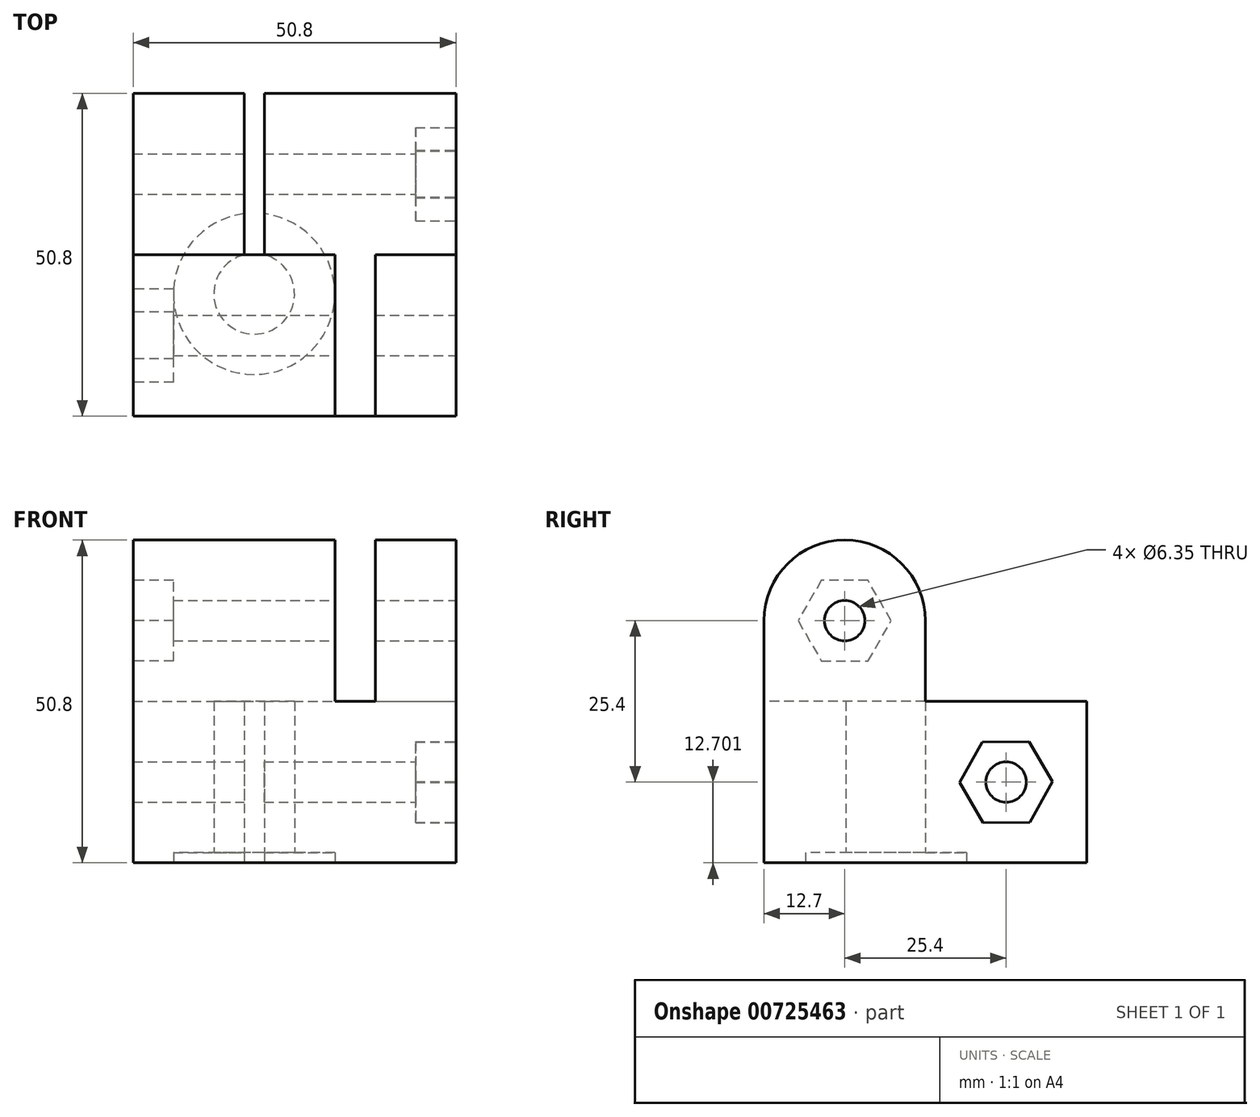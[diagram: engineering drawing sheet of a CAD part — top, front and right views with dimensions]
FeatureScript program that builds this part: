
annotation { "Feature Type Name" : "Feature", "Feature Type Description" : "" }
export const myFeature = defineFeature(function(context is Context, id is Id, definition is map)
    precondition{}
    {
        {
            var Q0;
            Q0=qCreatedBy(makeId("Front.planeOp"),FACE);
            var sketch = newSketch(context, id + "F0", { "sketchPlane" : qUnion([Q0])});
            skLineSegment(sketch, "E0.bottom", {"start": v(-27.31, 27.37) * mm, "end": v(23.49, 27.37) * mm});
            skLineSegment(sketch, "E0.top", {"start": v(-27.31, -23.43) * mm, "end": v(23.49, -23.43) * mm});
            skLineSegment(sketch, "E0.left", {"start": v(-27.31, 27.37) * mm, "end": v(-27.31, -23.43) * mm});
            skLineSegment(sketch, "E0.right", {"start": v(23.49, 27.37) * mm, "end": v(23.49, -23.43) * mm});
            skSolve(sketch);
        }
        {
            var Q0;
            Q0=makeQuery(id+"F0.imprint","IMPRINT",FACE,{"disambiguationData":[TD([[makeQuery(id+"F0.imprint","IMPRINT",EDGE,{"derivedFrom":sQuery(id+"F0.wireOp",EDGE,"E0.bottom")}),-1.0]])]});
            extrude(context, id + "F1", {"entities" : qUnion([Q0]), "endBound" : BoundingType.SYMMETRIC, "depth" : 50.8 * mm, "offsetDistance" : 25.4 * mm});
        }
        {
            var Q0;
            Q0=makeQuery(id+"F1.opExtrude","SWEPT_FACE",FACE,{"disambiguationData":[OSD([sQuery(id+"F0.wireOp",EDGE,"E0.top")])]});
            var sketch = newSketch(context, id + "F2", { "sketchPlane" : qUnion([Q0])});
            skArc(sketch, "E1", {"start": v(-6.67, 0) * mm, "mid": v(-8.26, 12.5) * mm, "end": v(-9.85, 0) * mm});
            skLineSegment(sketch, "E2.top", {"start": v(-9.85, -25.4) * mm, "end": v(-6.67, -25.4) * mm});
            skLineSegment(sketch, "E2.left", {"start": v(-9.85, 0) * mm, "end": v(-9.85, -25.4) * mm});
            skLineSegment(sketch, "E2.right", {"start": v(-6.67, 0) * mm, "end": v(-6.67, -25.4) * mm});
            skCircle(sketch, "E3", {"center": v(-8.26, 6.15) * mm, "radius": 12.7 * mm});
            skSolve(sketch);
        }
        {
            var Q0;
            Q0=makeQuery(id+"F2.imprint","IMPRINT",FACE,{"disambiguationData":[TD([[makeQuery(id+"F2.imprint","IMPRINT",EDGE,{"derivedFrom":sQuery(id+"F2.wireOp",EDGE,"E1")}),1.0]])]});
            var Q1;
            {var subQ0=sQuery(id+"F2.wireOp",EDGE,"E2.top");Q1=makeQuery(id+"F2.imprint","IMPRINT",FACE,{"disambiguationData":[TD([[makeQuery(id+"F2.imprint","IMPRINT",EDGE,{"derivedFrom":subQ0}),1.0]])]});}
            extrude(context, id + "F3", {"entities" : qUnion([Q0, Q1]), "operationType" : NewBodyOperationType.REMOVE, "oppositeDirection" : true, "depth" : 25.4 * mm, "offsetDistance" : 25.4 * mm});
        }
        {
            var Q0;
            Q0=makeQuery(id+"F1.opExtrude","SWEPT_FACE",FACE,{"disambiguationData":[OSD([sQuery(id+"F0.wireOp",EDGE,"E0.right")])]});
            var sketch = newSketch(context, id + "F4", { "sketchPlane" : qUnion([Q0])});
            skLineSegment(sketch, "E4", {"start": v(-36.89, 1.97) * mm, "end": v(-36.89, 33.76) * mm});
            skLineSegment(sketch, "E5", {"start": v(-36.89, 33.76) * mm, "end": v(34.59, 33.76) * mm});
            skLineSegment(sketch, "E6", {"start": v(34.59, 33.76) * mm, "end": v(34.59, 1.97) * mm});
            skArc(sketch, "E7", {"start": v(0, 14.67) * mm, "mid": v(-12.7, 27.37) * mm, "end": v(-25.4, 14.67) * mm});
            skLineSegment(sketch, "E8", {"start": v(-25.4, 1.97) * mm, "end": v(-25.4, 14.67) * mm});
            skLineSegment(sketch, "E9", {"start": v(0, 1.97) * mm, "end": v(0, 14.67) * mm});
            skLineSegment(sketch, "E10", {"start": v(-36.89, 1.97) * mm, "end": v(34.59, 1.97) * mm});
            skPoint(sketch, "E11.orphan", {"position": v(-25.4, 0) * mm});
            skPoint(sketch, "E12.orphan", {"position": v(34.59, 0) * mm});
            skCircle(sketch, "E13", {"center": v(-12.7, 14.67) * mm, "radius": 3.18 * mm});
            skCircle(sketch, "E14", {"center": v(12.7, -10.73) * mm, "radius": 3.18 * mm});
            skCircle(sketch, "E15.cCircle", {"center": v(12.7, -10.73) * mm, "radius": 6.35 * mm, "construction": true});
            skLineSegment(sketch, "E15.0", {"start": v(20.03, -10.66) * mm, "end": v(16.43, -17.04) * mm});
            skLineSegment(sketch, "E15.1", {"start": v(16.43, -17.04) * mm, "end": v(9.1, -17.11) * mm});
            skLineSegment(sketch, "E15.2", {"start": v(9.1, -17.11) * mm, "end": v(5.37, -10.8) * mm});
            skLineSegment(sketch, "E15.3", {"start": v(5.37, -10.8) * mm, "end": v(8.97, -4.41) * mm});
            skLineSegment(sketch, "E15.4", {"start": v(8.97, -4.41) * mm, "end": v(16.3, -4.34) * mm});
            skLineSegment(sketch, "E15.5", {"start": v(16.3, -4.34) * mm, "end": v(20.03, -10.66) * mm});
            skPoint(sketch, "E15.0.midPoint", {"position": v(18.23, -13.85) * mm});
            skSolve(sketch);
        }
        {
            var Q0;
            Q0=makeQuery(id+"F4.imprint","IMPRINT",FACE,{"disambiguationData":[TD([[makeQuery(id+"F4.imprint","IMPRINT",EDGE,{"derivedFrom":sQuery(id+"F4.wireOp",EDGE,"nHS85Hnr-vWbH-LP3G-OHDl-IovvBqo1vg3n")}),-1.0]])]});
            var Q1;
            {var subQ0=sQuery(id+"F4.wireOp",EDGE,"E7");var subQ1=sQuery(id+"F0.wireOp",EDGE,"E0.right");var subQ2=makeQuery(id+"F1.opExtrude","CAP_EDGE",EDGE,{"disambiguationData":[OSD([subQ1])],"isStart":false});var subQ3=makeQuery(id+"F4.imprint","INTERSECT",VERTEX,{"derivedFrom":[subQ2,subQ0,sQuery(id+"F4.wireOp",EDGE,"E8")]});Q1=makeQuery(id+"F4.imprint","IMPRINT",FACE,{"disambiguationData":[TD([[makeQuery(id+"F4.imprint","IMPRINT",EDGE,{"disambiguationData":[TD([[subQ3,1.0]])],"derivedFrom":subQ0}),-1.0]])]});}
            var Q2;
            {var subQ0=sQuery(id+"F4.wireOp",EDGE,"E9");Q2=makeQuery(id+"F4.imprint","IMPRINT",FACE,{"disambiguationData":[TD([[makeQuery(id+"F4.imprint","IMPRINT",EDGE,{"derivedFrom":subQ0}),-1.0]])]});}
            var Q3;
            Q3=makeQuery(id+"F4.imprint","IMPRINT",FACE,{"disambiguationData":[TD([[makeQuery(id+"F4.imprint","IMPRINT",EDGE,{"derivedFrom":sQuery(id+"F4.wireOp",EDGE,"E13")}),1.0]])]});
            var Q4;
            Q4=makeQuery(id+"F4.imprint","IMPRINT",FACE,{"disambiguationData":[TD([[makeQuery(id+"F4.imprint","IMPRINT",EDGE,{"derivedFrom":sQuery(id+"F4.wireOp",EDGE,"E14")}),1.0]])]});
            extrude(context, id + "F5", {"entities" : qUnion([Q0, Q1, Q2, Q3, Q4]), "operationType" : NewBodyOperationType.REMOVE, "endBound" : BoundingType.THROUGH_ALL, "oppositeDirection" : true, "depth" : 50.8 * mm, "offsetDistance" : 25.4 * mm});
        }
        {
            var Q0;
            Q0=makeQuery(id+"F1.opExtrude","CAP_FACE",FACE,{"disambiguationData":[OSD([sQuery(id+"F0.wireOp",EDGE,"E0.bottom"),sQuery(id+"F0.wireOp",EDGE,"E0.top"),sQuery(id+"F0.wireOp",EDGE,"E0.left"),sQuery(id+"F0.wireOp",EDGE,"E0.right")])],"isStart":false});
            var sketch = newSketch(context, id + "F6", { "sketchPlane" : qUnion([Q0])});
            skLineSegment(sketch, "E16.bottom", {"start": v(4.44, 1.97) * mm, "end": v(10.79, 1.97) * mm});
            skLineSegment(sketch, "E16.top", {"start": v(4.44, 44.67) * mm, "end": v(10.79, 44.67) * mm});
            skLineSegment(sketch, "E16.left", {"start": v(4.44, 1.97) * mm, "end": v(4.44, 44.67) * mm});
            skLineSegment(sketch, "E16.right", {"start": v(10.79, 1.97) * mm, "end": v(10.79, 44.67) * mm});
            skSolve(sketch);
        }
        {
            var Q0;
            {var subQ0=sQuery(id+"F6.wireOp",EDGE,"E16.top");Q0=makeQuery(id+"F6.imprint","IMPRINT",FACE,{"disambiguationData":[TD([[makeQuery(id+"F6.imprint","IMPRINT",EDGE,{"derivedFrom":subQ0}),-1.0]])]});}
            var Q1;
            {var subQ0=sQuery(id+"F6.wireOp",EDGE,"E16.bottom");Q1=makeQuery(id+"F6.imprint","IMPRINT",FACE,{"disambiguationData":[TD([[makeQuery(id+"F6.imprint","IMPRINT",EDGE,{"derivedFrom":subQ0}),1.0]])]});}
            extrude(context, id + "F7", {"entities" : qUnion([Q0, Q1]), "operationType" : NewBodyOperationType.REMOVE, "endBound" : BoundingType.THROUGH_ALL, "oppositeDirection" : true, "depth" : 25.4 * mm, "offsetDistance" : 25.4 * mm});
        }
        {
            var Q0;
            Q0=makeQuery(id+"F1.opExtrude","SWEPT_FACE",FACE,{"disambiguationData":[OSD([sQuery(id+"F0.wireOp",EDGE,"E0.left")])]});
            var sketch = newSketch(context, id + "F8", { "sketchPlane" : qUnion([Q0])});
            skCircle(sketch, "E17.cCircle", {"center": v(12.7, 14.67) * mm, "radius": 6.35 * mm, "construction": true});
            skLineSegment(sketch, "E17.0", {"start": v(5.37, 14.67) * mm, "end": v(9.03, 21.02) * mm});
            skLineSegment(sketch, "E17.1", {"start": v(9.03, 21.02) * mm, "end": v(16.37, 21.02) * mm});
            skLineSegment(sketch, "E17.2", {"start": v(16.37, 21.02) * mm, "end": v(20.03, 14.67) * mm});
            skLineSegment(sketch, "E17.3", {"start": v(20.03, 14.67) * mm, "end": v(16.37, 8.32) * mm});
            skLineSegment(sketch, "E17.4", {"start": v(16.37, 8.32) * mm, "end": v(9.03, 8.32) * mm});
            skLineSegment(sketch, "E17.5", {"start": v(9.03, 8.32) * mm, "end": v(5.37, 14.67) * mm});
            skPoint(sketch, "E17.0.midPoint", {"position": v(7.2, 17.85) * mm});
            skSolve(sketch);
        }
        {
            var Q0;
            Q0=makeQuery(id+"F8.imprint","IMPRINT",FACE,{"disambiguationData":[TD([[makeQuery(id+"F8.imprint","IMPRINT",EDGE,{"derivedFrom":sQuery(id+"F8.wireOp",EDGE,"E17.0")}),-1.0]])]});
            extrude(context, id + "F9", {"entities" : qUnion([Q0]), "operationType" : NewBodyOperationType.REMOVE, "oppositeDirection" : true, "depth" : 6.35 * mm, "offsetDistance" : 25.4 * mm});
        }
        {
            var Q0;
            Q0=makeQuery(id+"F4.imprint","IMPRINT",FACE,{"disambiguationData":[TD([[makeQuery(id+"F4.imprint","IMPRINT",EDGE,{"derivedFrom":sQuery(id+"F4.wireOp",EDGE,"E14")}),-1.0]])]});
            extrude(context, id + "F10", {"entities" : qUnion([Q0]), "operationType" : NewBodyOperationType.REMOVE, "oppositeDirection" : true, "depth" : 6.35 * mm, "offsetDistance" : 25.4 * mm});
        }
        {
            var Q0;
            {var subQ5=sQuery(id+"F2.wireOp",EDGE,"E1");Q0=makeQuery(id+"F2.imprint","IMPRINT",FACE,{"disambiguationData":[TD([[makeQuery(id+"F2.imprint","IMPRINT",EDGE,{"derivedFrom":subQ5}),-1.0]])]});}
            extrude(context, id + "F11", {"entities" : qUnion([Q0]), "operationType" : NewBodyOperationType.REMOVE, "oppositeDirection" : true, "depth" : 1.59 * mm, "offsetDistance" : 25.4 * mm});
        }
    });
